# Revit family: 447-DN080-RFA_2018
name_source: partatom
category: Pipe Accessories
revit_build: Autodesk Revit LT 2018 (Build: 20180329_1100(x64)
units: mm (PartAtom-declared; Revit-internal decimal feet)

## family parameters
Always vertical = Yes
Cut with Voids When Loaded = No
Part Type = Valve - Breaks Into
Round Connector Dimension = Use Diameter
Shared = No
Work Plane-Based = No

## types (10) — shared parameters
CAT0 = Yes
L2D = 350 mm
L2D_Min = 3048 mm
Manufacturer = Hydronix
QmdConnectorList = 301;D;302;D
Type Comments = přírubový; PN16; -10~+120°C
URL = http://www.hydronix.cz
W2D = 100 mm
magiPartTypeId = 304
magiProductFamilyId = b72cb932c1b3471491e3d369876ba1

## per-type parameters (varying)
| type | C | C1 | CC | D | DT | Description | FD | HH1 | L2 | LM | LM1 | MC Product Code | S | X1 | X2 | magiProductId |
| 447-DN100 | 35 mm  [stored 0.114829 ft] | 32 mm  [stored 0.104987 ft] | 4 mm  [stored 0.0131234 ft] | 100 mm | 130 mm | Ruční vyvažovací ventil přírubový; DN100; PN16; kvs184,7 | 220 mm | 218 mm | 175 mm | 280 mm | 28 mm  [stored 0.0918635 ft] | 447 100 (DN100; PN16 kvs184,7) | 156 mm | 49 mm  [stored 0.160761 ft] | 79 mm | 98b46d48787042dd9a812fc0797c69 |
| 447-DN125 | 40 mm  [stored 0.131234 ft] | 36 mm  [stored 0.11811 ft] | 4 mm  [stored 0.0131234 ft] | 125 mm | 130 mm | Ruční vyvažovací ventil přírubový; DN125; PN16; kvs285,1 | 250 mm | 238 mm | 200 mm | 320 mm | 32 mm  [stored 0.104987 ft] | 447 125 (DN125; PN16 kvs285,1) | 184 mm | 56 mm  [stored 0.183727 ft] | 87 mm | 02b47ccb17f74d08923d86f3fe118e |
| 447-DN150 | 48 mm  [stored 0.15748 ft] | 43 mm | 5 mm  [stored 0.0164042 ft] | 150 mm | 130 mm | Ruční vyvažovací ventil přírubový; DN150; PN16; kvs390,2 | 285 mm | 263 mm | 240 mm | 384 mm | 38 mm | 447 150 (DN150; PN16 kvs390,2) | 211 mm | 67 mm | 96 mm | 7f7b5672e2b748ca8839732ddacd1d |
| 447-DN200 | 60 mm  [stored 0.19685 ft] | 54 mm  [stored 0.177165 ft] | 6 mm  [stored 0.019685 ft] | 200 mm | 310 mm | Ruční vyvažovací ventil přírubový; DN200; PN16; kvs710 | 340 mm | 427 mm | 300 mm | 480 mm | 48 mm  [stored 0.15748 ft] | 447 200 (DN200; PN16 kvs710) | 266 mm | 84 mm  [stored 0.275591 ft] | 155 mm | e1019e6fc9b647ceac6d31797e2f53 |
| 447-DN250 | 73 mm  [stored 0.239501 ft] | 66 mm  [stored 0.216535 ft] | 7 mm | 250 mm | 310 mm | Ruční vyvažovací ventil přírubový; DN250; PN16; kvs1188 | 405 mm | 472 mm | 365 mm | 584 mm | 58 mm | 447 250 (DN250; PN16 kvs1188) | 319 mm | 102 mm | 172 mm | a0eac83e29f84220b7ba68901aa49e |
| 447-DN300 | 85 mm  [stored 0.278871 ft] | 77 mm | 9 mm | 300 mm | 310 mm | Ruční vyvažovací ventil přírubový; DN300; PN16; kvs1504 | 460 mm | 482 mm | 425 mm | 680 mm | 68 mm  [stored 0.223097 ft] | 447 300 (DN300; PN16 kvs1504) | 370 mm | 119 mm | 175 mm | 476300b2e87f4f20bd49d272c44436 |
| 447-DN040 | 20 mm  [stored 0.0656168 ft] | 18 mm  [stored 0.0590551 ft] | 2 mm  [stored 0.00656168 ft] | 40 mm | 74 mm  [stored 0.242782 ft] | Ruční vyvažovací ventil přírubový; DN40; PN16; kvs22,36 | 150 mm | 117 mm | 100 mm | 160 mm | 16 mm  [stored 0.0524934 ft] | 447 040 (DN40; PN16 kvs22,36) | 84 mm  [stored 0.275591 ft] | 28 mm  [stored 0.0918635 ft] | 43 mm | 1b02107dafeb4f5588628c478854c2 |
| 447-DN050 | 23 mm  [stored 0.0754593 ft] | 21 mm | 2 mm  [stored 0.00656168 ft] | 50 mm | 74 mm  [stored 0.242782 ft] | Ruční vyvažovací ventil přírubový; DN50; PN16; kvs32,15 | 165 mm | 117 mm | 115 mm | 184 mm | 18 mm  [stored 0.0590551 ft] | 447 050 (DN50; PN16 kvs32,15) | 99 mm | 32 mm  [stored 0.104987 ft] | 43 mm | 5ed7087ff739473a8b86e2dbbe5062 |
| 447-DN065 | 29 mm  [stored 0.0951444 ft] | 26 mm | 3 mm  [stored 0.00984252 ft] | 65 mm | 130 mm | Ruční vyvažovací ventil přírubový; DN65; PN16; kvs88,8 | 185 mm | 198 mm | 145 mm | 232 mm | 23 mm  [stored 0.0754593 ft] | 447 065 (DN65; PN16 kvs88,8) | 118 mm | 41 mm | 72 mm | bd77367604f142d88050bf73c88c7b |
| 447-DN080 | 31 mm  [stored 0.101706 ft] | 28 mm  [stored 0.0918635 ft] | 3 mm  [stored 0.00984252 ft] | 80 mm | 130 mm | Ruční vyvažovací ventil přírubový; DN80; PN16; kvs113,4 | 200 mm | 198 mm | 155 mm | 248 mm | 25 mm  [stored 0.082021 ft] | 447 080 (DN80; PN16 kvs113,4) | 132 mm | 43 mm | 72 mm | 7399fcf493614c92ad9035a8ac3adf |

note: [stored X ft] marks values corroborated as IEEE doubles in the binary element streams (Revit-internal decimal feet)

## geometry (parser evidence)
native form markers: Sweep x1
no freeform markers — native parametric forms only
